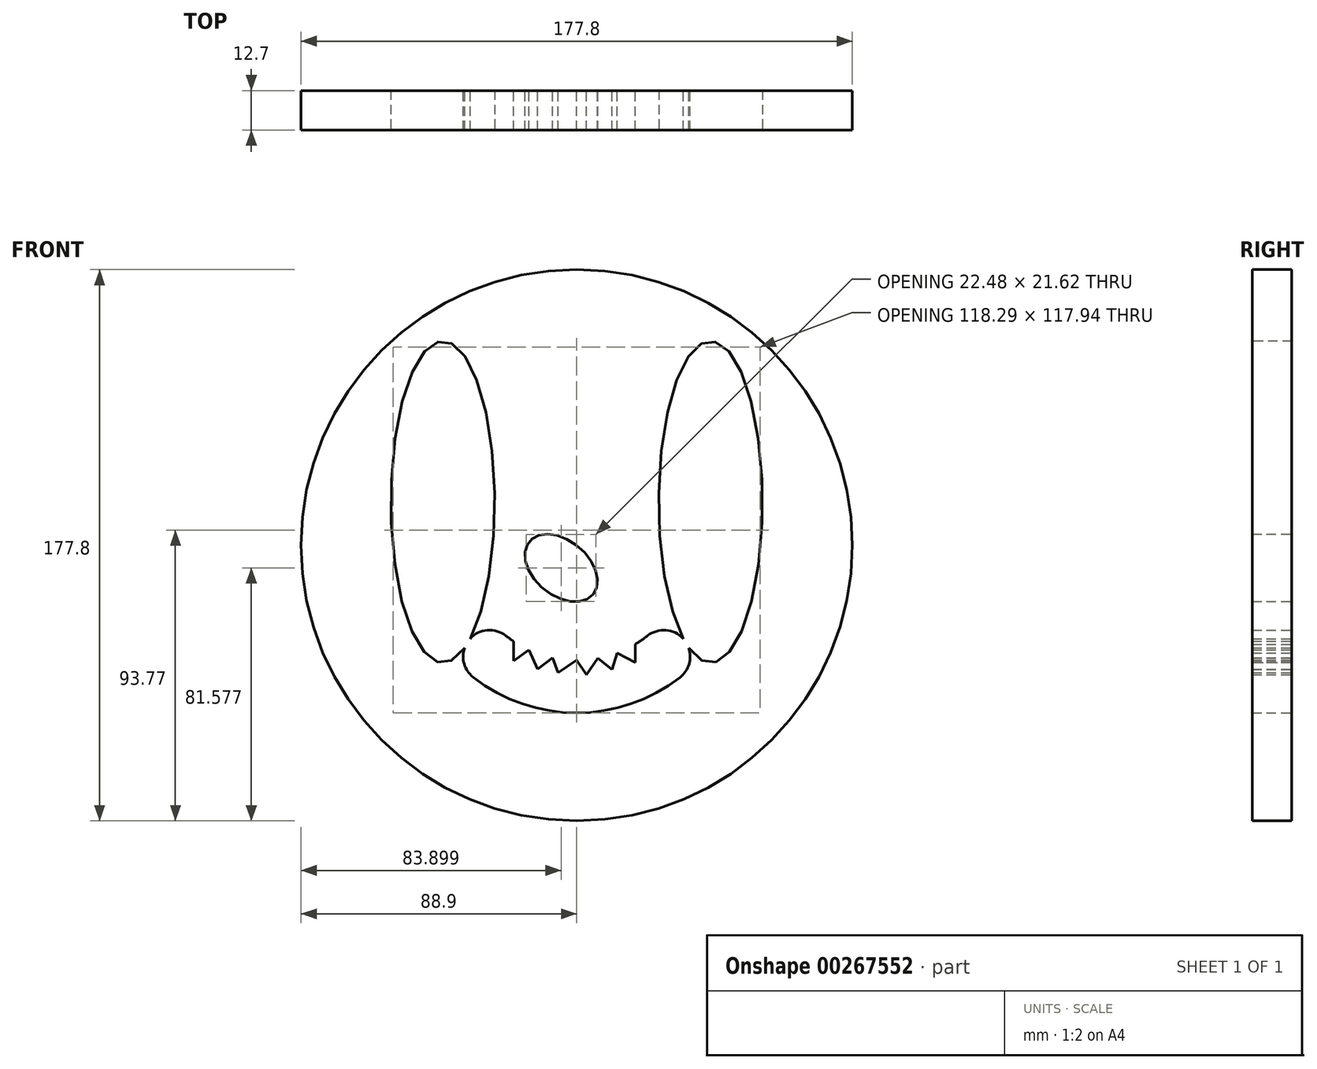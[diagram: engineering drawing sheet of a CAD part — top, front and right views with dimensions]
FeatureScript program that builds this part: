
annotation { "Feature Type Name" : "Feature", "Feature Type Description" : "" }
export const myFeature = defineFeature(function(context is Context, id is Id, definition is map)
    precondition{}
    {
        {
            var Q0;
            Q0=qCreatedBy(makeId("Front.planeOp"),FACE);
            var sketch = newSketch(context, id + "F0", { "sketchPlane" : qUnion([Q0])});
            skCircle(sketch, "E0", {"center": v(0, 120.65) * mm, "radius": 88.9 * mm});
            skEllipse(sketch, "E1", {"center": v(-43.19, 134.6) * mm, "majorRadius": 51.86 * mm, "minorRadius": 16.73 * mm, "majorAxis": v(0, -1)});
            skEllipse(sketch, "E2.MirrorC", {"center": v(43.19, 134.6) * mm, "majorRadius": 51.86 * mm, "minorRadius": 16.73 * mm, "majorAxis": v(0, -1)});
            skArc(sketch, "E3.0", {"start": v(-33.35, 78.05) * mm, "mid": v(0, 66.55) * mm, "end": v(33.35, 78.05) * mm});
            skArc(sketch, "E4.0", {"start": v(-22.86, 91.45) * mm, "mid": v(-21.64, 90.54) * mm, "end": v(-20.4, 89.68) * mm});
            skArc(sketch, "E5", {"start": v(-22.86, 91.45) * mm, "mid": v(-34.8, 90) * mm, "end": v(-33.35, 78.05) * mm});
            skArc(sketch, "E6", {"start": v(33.35, 78.05) * mm, "mid": v(34.8, 90) * mm, "end": v(22.86, 91.45) * mm});
            skLineSegment(sketch, "E7", {"start": v(18.85, 88.71) * mm, "end": v(18.85, 82.79) * mm});
            skLineSegment(sketch, "E8", {"start": v(18.85, 82.79) * mm, "end": v(13, 85.92) * mm});
            skLineSegment(sketch, "E9", {"start": v(13, 85.92) * mm, "end": v(11.45, 80.59) * mm});
            skLineSegment(sketch, "E10", {"start": v(11.45, 80.59) * mm, "end": v(6.8, 84.2) * mm});
            skLineSegment(sketch, "E11", {"start": v(6.8, 84.2) * mm, "end": v(3.15, 78.91) * mm});
            skLineSegment(sketch, "E12", {"start": v(3.15, 78.91) * mm, "end": v(0, 83.57) * mm});
            skLineSegment(sketch, "E13", {"start": v(0, 83.57) * mm, "end": v(-6, 79.52) * mm});
            skLineSegment(sketch, "E14", {"start": v(-6, 79.52) * mm, "end": v(-7.8, 84.4) * mm});
            skLineSegment(sketch, "E15", {"start": v(-7.8, 84.4) * mm, "end": v(-12.6, 80.69) * mm});
            skLineSegment(sketch, "E16", {"start": v(-12.6, 80.69) * mm, "end": v(-15.35, 86.9) * mm});
            skLineSegment(sketch, "E17", {"start": v(-15.35, 86.9) * mm, "end": v(-20.4, 83.36) * mm});
            skLineSegment(sketch, "E18", {"start": v(-20.4, 83.36) * mm, "end": v(-20.4, 89.68) * mm});
            skArc(sketch, "E19.trimOffspring", {"start": v(18.85, 88.71) * mm, "mid": v(20.9, 90.02) * mm, "end": v(22.86, 91.45) * mm});
            skEllipse(sketch, "E20", {"center": v(46.05, 140.35) * mm, "majorRadius": 11.93 * mm, "minorRadius": 3.27 * mm, "majorAxis": v(0, -1)});
            skEllipse(sketch, "E21", {"center": v(-46.29, 124.54) * mm, "majorRadius": 10.52 * mm, "minorRadius": 2.38 * mm, "majorAxis": v(0.3, 0.96)});
            skEllipse(sketch, "E22", {"center": v(-5, 113.33) * mm, "majorRadius": 13.31 * mm, "minorRadius": 8.84 * mm, "majorAxis": v(0.77, -0.64)});
            skSolve(sketch);
        }
        {
            var Q0;
            Q0=makeQuery(id+"F0.imprint","IMPRINT",FACE,{"disambiguationData":[TD([[makeQuery(id+"F0.imprint","IMPRINT",EDGE,{"derivedFrom":sQuery(id+"F0.wireOp",EDGE,"E0")}),1.0]])]});
            extrude(context, id + "F1", {"entities" : qUnion([Q0]), "depth" : 12.7 * mm});
        }
    });
